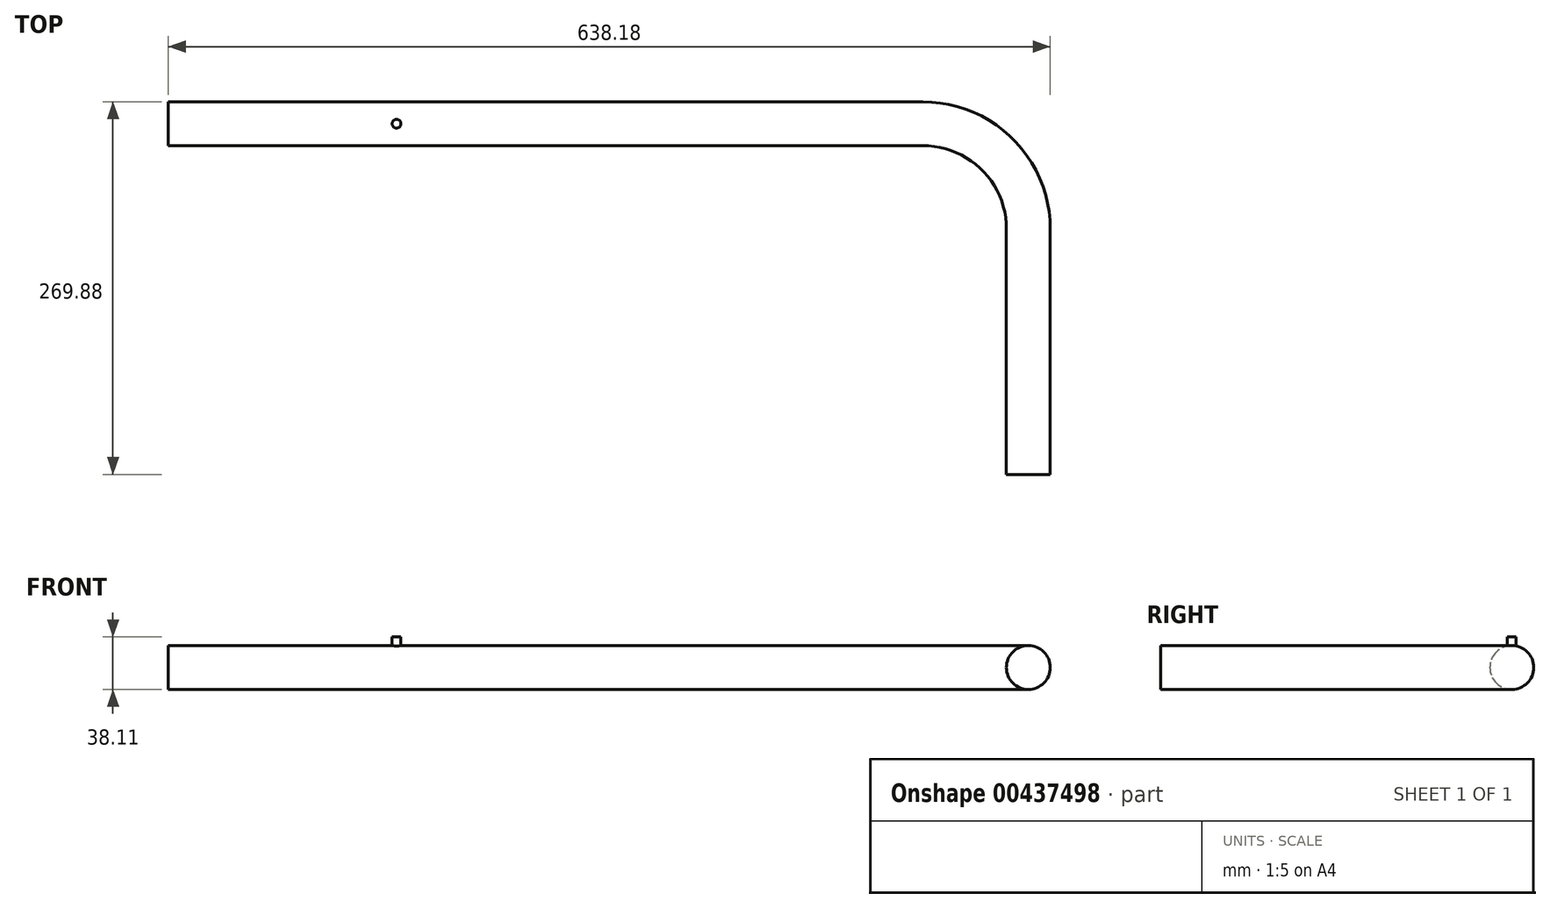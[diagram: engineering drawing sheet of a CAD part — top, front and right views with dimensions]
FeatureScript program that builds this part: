
annotation { "Feature Type Name" : "Feature", "Feature Type Description" : "" }
export const myFeature = defineFeature(function(context is Context, id is Id, definition is map)
    precondition{}
    {
        {
            var Q0;
            Q0=qCreatedBy(makeId("Top.planeOp"),FACE);
            var sketch = newSketch(context, id + "F0", { "sketchPlane" : qUnion([Q0])});
            skArc(sketch, "E0", {"start": v(406.4, -76.2) * mm, "mid": v(384.08, -22.32) * mm, "end": v(330.2, 0) * mm});
            skLineSegment(sketch, "E1", {"start": v(406.4, -76.2) * mm, "end": v(406.4, -254) * mm});
            skLineSegment(sketch, "E2", {"start": v(0, 0) * mm, "end": v(330.2, 0) * mm});
            skLineSegment(sketch, "E3", {"start": v(0, 0) * mm, "end": v(-152.4, 0) * mm});
            skSolve(sketch);
        }
        {
            var Q0;
            Q0=qCreatedBy(makeId("Front.planeOp"),FACE);
            cPlane(context, id + "F1", {"entities" : qUnion([Q0]), "cplaneType" : CPlaneType.OFFSET, "offset" : 254 * mm, "width" : 152.4 * mm, "height" : 152.4 * mm});
        }
        {
            var Q0;
            Q0=qCreatedBy(id+"F1.planeOp",FACE);
            var sketch = newSketch(context, id + "F2", { "sketchPlane" : qUnion([Q0])});
            skCircle(sketch, "E4", {"center": v(406.4, 0) * mm, "radius": 15.88 * mm});
            skSolve(sketch);
        }
        {
            var Q0;
            Q0=makeQuery(id+"F2.imprint","IMPRINT",FACE,{"disambiguationData":[TD([[makeQuery(id+"F2.imprint","IMPRINT",EDGE,{"derivedFrom":sQuery(id+"F2.wireOp",EDGE,"E4")}),1.0]])]});
            var Q1;
            Q1=sQuery(id+"F0.wireOp",EDGE,"E2");
            var Q2;
            Q2=sQuery(id+"F0.wireOp",EDGE,"E0");
            var Q3;
            Q3=sQuery(id+"F0.wireOp",EDGE,"E1");
            var Q4;
            Q4=sQuery(id+"F0.wireOp",EDGE,"E3");
            sweep(context, id + "F3", {"profiles" : qUnion([Q0]), "path" : qUnion([Q1, Q2, Q3, Q4])});
        }
        {
            var Q0;
            Q0=qCreatedBy(makeId("Top.planeOp"),FACE);
            var sketch = newSketch(context, id + "F4", { "sketchPlane" : qUnion([Q0])});
            skCircle(sketch, "E5", {"center": v(-50.8, 0) * mm, "radius": 3.18 * mm});
            skSolve(sketch);
        }
        {
            var Q0;
            Q0 = qSketchRegion(id + "F4", true);
            extrude(context, id + "F5", {"entities" : qUnion([Q0]), "operationType" : NewBodyOperationType.ADD, "depth" : 22.22 * mm});
        }
        {
            var Q0;
            Q0=makeQuery(id+"F3.opSweep","CAP_FACE",FACE,{"disambiguationData":[OSD([sQuery(id+"F0.wireOp",VERTEX,"E3.end"),sQuery(id+"F2.wireOp",EDGE,"E4")])],"isStart":false});
            var sketch = newSketch(context, id + "F6", { "sketchPlane" : qUnion([Q0])});
            skCircle(sketch, "E6", {"center": v(0, 0) * mm, "radius": 15.88 * mm});
            skSolve(sketch);
        }
        {
            var Q0;
            Q0 = qSketchRegion(id + "F6", true);
            extrude(context, id + "F7", {"entities" : qUnion([Q0]), "operationType" : NewBodyOperationType.ADD, "depth" : 63.5 * mm, "offsetDistance" : 25.4 * mm});
        }
    });
